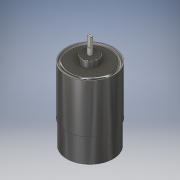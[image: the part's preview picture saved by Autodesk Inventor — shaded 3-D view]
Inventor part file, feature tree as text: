
AUTODESK INVENTOR PART (.ipt)
format: ipt  version: 2016 (Build 200138000, 138)  size: 179,712 bytes
history: native  units: in
note: dims shown in document units (in); Inventor stores cm internally (conversion verified against a paired STEP export)
features: extrude x5, sketch x5, fillet x3
ambient origin geometry x8: Origin, YZ Plane, XZ Plane, XY Plane, X Axis, Y Axis, Z Axis, Center Point
bodies: Solid1 (feature_tree)
feature tree (13):
  extrude  "Extrusion1"  Depth=2.23in TaperAngle=0.0deg
  extrude  "Extrusion2"  Depth=0.19in TaperAngle=0.0deg
  extrude  "Extrusion3"  Depth=0.2in TaperAngle=0.0deg
  extrude  "Extrusion4"  Depth=0.05in
  fillet  "Fillet1"  Radius=0.1in
  fillet  "Fillet2"  Radius=0.02in
  fillet  "Fillet3"  Radius=1.41in
  extrude  "Extrusion5"  Depth=1.488in TaperAngle=0.0deg
  sketch  "Sketch1"  dims[d0=1.41in d1=2.23in d2=0.0in]
  sketch  "Sketch2"  dims[d3=0.515in d4=0.19in d5=0.0in]
  sketch  "Sketch3"  dims[d6=0.128in d7=0.2in d8=0.0in]
  sketch  "Sketch4"  dims[d11=0.32in d12=0.0in d13=0.05in d14=0.1in d15=0.02in d17=1.41in]
  sketch  "Sketch5"  dims[d18=0.025in d19=1.488in d20=0.0in]
